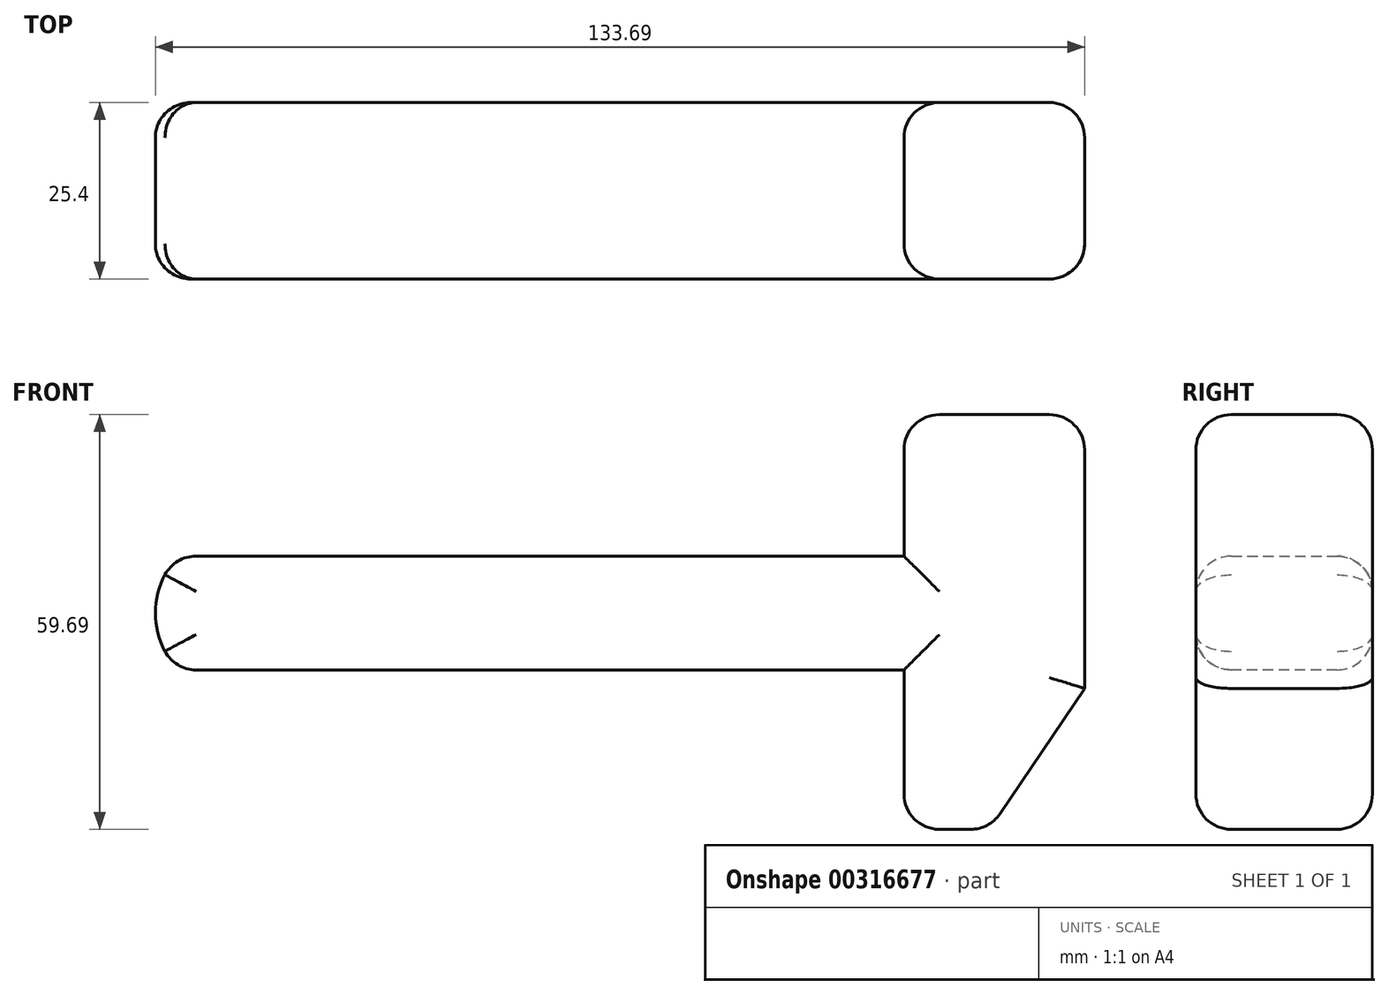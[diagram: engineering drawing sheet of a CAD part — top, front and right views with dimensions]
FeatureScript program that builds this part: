
annotation { "Feature Type Name" : "Feature", "Feature Type Description" : "" }
export const myFeature = defineFeature(function(context is Context, id is Id, definition is map)
    precondition{}
    {
        {
            var Q0;
            Q0=qCreatedBy(makeId("Front.planeOp"),FACE);
            var sketch = newSketch(context, id + "F0", { "sketchPlane" : qUnion([Q0])});
            skLineSegment(sketch, "E0", {"start": v(55.4, -8.18) * mm, "end": v(-48.94, -8.18) * mm});
            skLineSegment(sketch, "E1.MirrorCS", {"start": v(55.4, 8.18) * mm, "end": v(-48.94, 8.18) * mm});
            skArc(sketch, "E2", {"start": v(-48.94, 8.18) * mm, "mid": v(-52.3, 0) * mm, "end": v(-48.94, -8.18) * mm});
            skLineSegment(sketch, "E3.bottom", {"start": v(55.4, 28.56) * mm, "end": v(81.39, 28.56) * mm});
            skLineSegment(sketch, "E3.left", {"start": v(55.4, 28.56) * mm, "end": v(55.4, -31.13) * mm});
            skLineSegment(sketch, "E3.right", {"start": v(81.39, 28.56) * mm, "end": v(81.39, -10.85) * mm});
            skLineSegment(sketch, "E4", {"start": v(81.39, -10.85) * mm, "end": v(67.68, -31.13) * mm});
            skLineSegment(sketch, "E5", {"start": v(67.68, -31.13) * mm, "end": v(55.4, -31.13) * mm});
            skSolve(sketch);
        }
        {
            var Q0;
            Q0 = qSketchRegion(id + "F0", true);
            extrude(context, id + "F1", {"entities" : qUnion([Q0]), "depth" : 25.4 * mm});
        }
        {
            var Q0;
            Q0=makeQuery(id+"F1.opExtrude","SWEPT_FACE",FACE,{"disambiguationData":[OSD([sQuery(id+"F0.wireOp",EDGE,"E5")])]});
            var Q1;
            Q1=makeQuery(id+"F1.opExtrude","CAP_FACE",FACE,{"disambiguationData":[OSD([sQuery(id+"F0.wireOp",EDGE,"E0"),sQuery(id+"F0.wireOp",EDGE,"E1.MirrorCS"),sQuery(id+"F0.wireOp",EDGE,"E2"),sQuery(id+"F0.wireOp",EDGE,"E3.bottom"),sQuery(id+"F0.wireOp",EDGE,"E3.left"),sQuery(id+"F0.wireOp",EDGE,"E3.right"),sQuery(id+"F0.wireOp",EDGE,"E4"),sQuery(id+"F0.wireOp",EDGE,"E5")])],"isStart":true});
            var Q2;
            Q2=makeQuery(id+"F1.opExtrude","CAP_FACE",FACE,{"disambiguationData":[OSD([sQuery(id+"F0.wireOp",EDGE,"E0"),sQuery(id+"F0.wireOp",EDGE,"E1.MirrorCS"),sQuery(id+"F0.wireOp",EDGE,"E2"),sQuery(id+"F0.wireOp",EDGE,"E3.bottom"),sQuery(id+"F0.wireOp",EDGE,"E3.left"),sQuery(id+"F0.wireOp",EDGE,"E3.right"),sQuery(id+"F0.wireOp",EDGE,"E4"),sQuery(id+"F0.wireOp",EDGE,"E5")])],"isStart":false});
            var Q3;
            Q3=makeQuery(id+"F1.opExtrude","SWEPT_FACE",FACE,{"disambiguationData":[OSD([sQuery(id+"F0.wireOp",EDGE,"E3.bottom")])]});
            fillet(context, id + "F2", {"entities" : qUnion([Q0, Q1, Q2, Q3]), "radius" : 5.08 * mm, "tangentPropagation" : true, "allowEdgeOverflow" : false});
        }
        {
            var Q0;
            Q0=makeQuery(id+"F1.opExtrude","SWEPT_FACE",FACE,{"disambiguationData":[OSD([sQuery(id+"F0.wireOp",EDGE,"E2")])]});
            var Q1;
            Q1=makeQuery(id+"F1.opExtrude","CAP_FACE",FACE,{"disambiguationData":[OSD([sQuery(id+"F0.wireOp",EDGE,"E0"),sQuery(id+"F0.wireOp",EDGE,"E1.MirrorCS"),sQuery(id+"F0.wireOp",EDGE,"E2"),sQuery(id+"F0.wireOp",EDGE,"E3.bottom"),sQuery(id+"F0.wireOp",EDGE,"E3.left"),sQuery(id+"F0.wireOp",EDGE,"E3.right"),sQuery(id+"F0.wireOp",EDGE,"E4"),sQuery(id+"F0.wireOp",EDGE,"E5")])],"isStart":false});
            fillet(context, id + "F3", {"entities" : qUnion([Q0, Q1]), "radius" : 5.08 * mm, "tangentPropagation" : true, "allowEdgeOverflow" : false});
        }
    });
